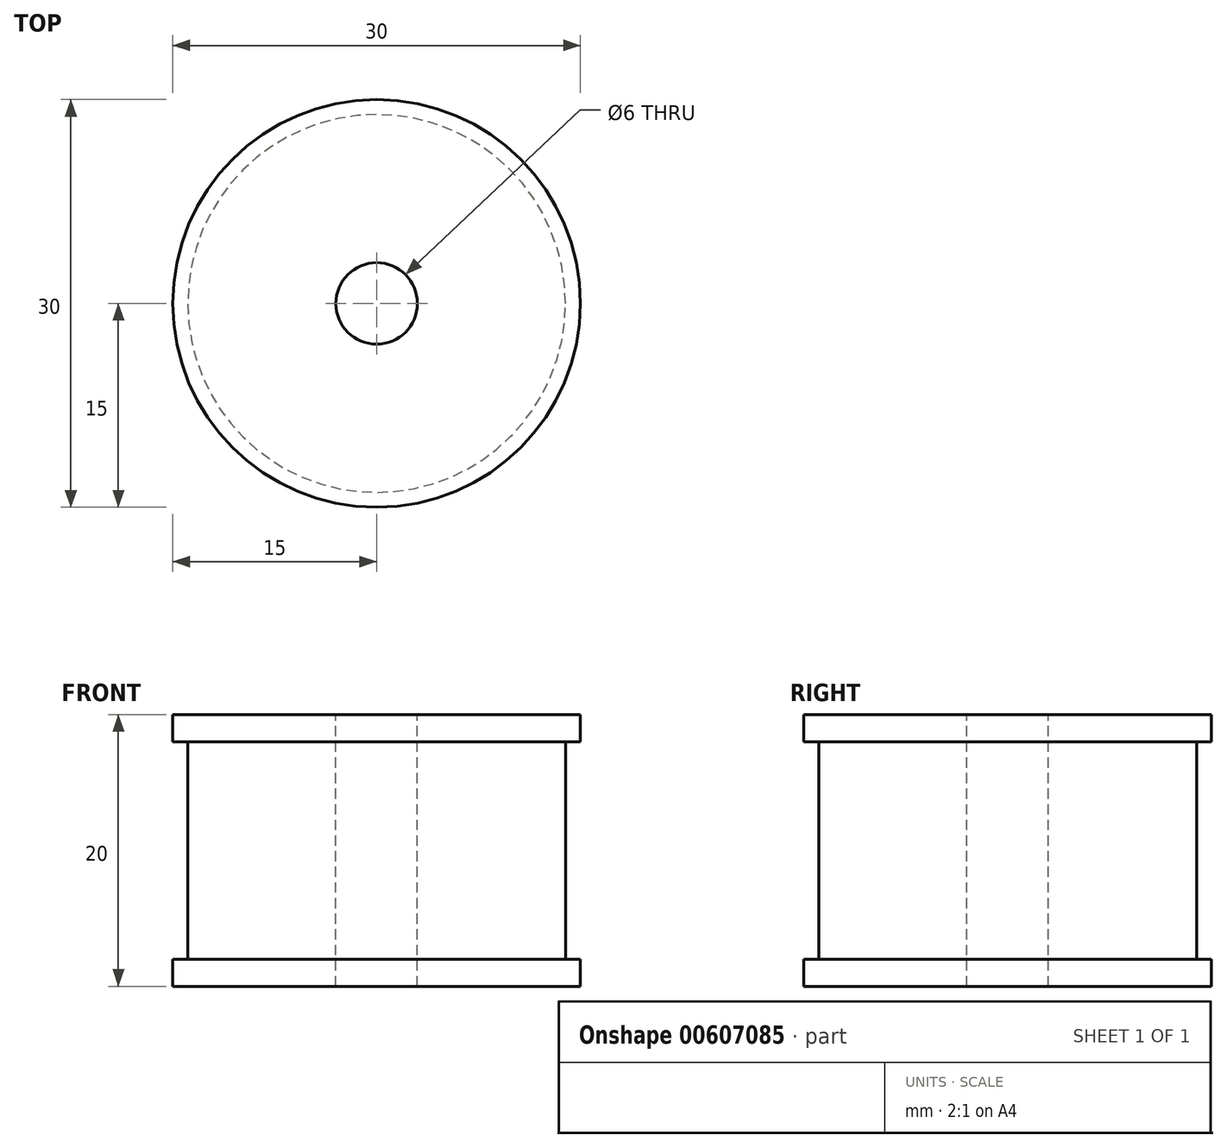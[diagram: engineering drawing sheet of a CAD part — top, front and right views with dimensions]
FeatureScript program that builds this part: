
annotation { "Feature Type Name" : "Feature", "Feature Type Description" : "" }
export const myFeature = defineFeature(function(context is Context, id is Id, definition is map)
    precondition{}
    {
        {
            var Q0;
            Q0=qCreatedBy(makeId("Top.planeOp"),FACE);
            var sketch = newSketch(context, id + "F0", { "sketchPlane" : qUnion([Q0]) });
            skCircle(sketch, "E0", {"center": v(0, 0) * mm, "radius": 13.9 * mm});
            skSolve(sketch);
        }
        {
            var Q0;
            Q0 = qSketchRegion(id + "F0", true);
            extrude(context, id + "F1", {"entities" : qUnion([Q0]), "depth" : 16 * mm, "offsetDistance" : 25 * mm});
        }
        {
            var Q0;
            Q0=makeQuery(id+"F1.opExtrude","CAP_FACE",FACE,{"disambiguationData":[OSD([sQuery(id+"F0.wireOp",EDGE,"E0")])],"isStart":false});
            var sketch = newSketch(context, id + "F2", { "sketchPlane" : qUnion([Q0]) });
            skCircle(sketch, "E1", {"center": v(0, 0) * mm, "radius": 15 * mm});
            skSolve(sketch);
        }
        {
            var Q0;
            Q0=makeQuery(id+"F2.imprint","IMPRINT",FACE,{"disambiguationData":[TD([[makeQuery(id+"F2.imprint","IMPRINT",EDGE,{"derivedFrom":makeQuery(id+"F1.opExtrude","CAP_EDGE",EDGE,{"disambiguationData":[OSD([sQuery(id+"F0.wireOp",EDGE,"E0")])],"isStart":false})}),1.0]])]});
            var Q1;
            Q1=makeQuery(id+"F2.imprint","IMPRINT",FACE,{"disambiguationData":[TD([[makeQuery(id+"F2.imprint","IMPRINT",EDGE,{"derivedFrom":sQuery(id+"F2.wireOp",EDGE,"E1")}),1.0]])]});
            extrude(context, id + "F3", {"entities" : qUnion([Q0, Q1]), "operationType" : NewBodyOperationType.ADD, "depth" : 2 * mm, "offsetDistance" : 25 * mm});
        }
        {
            var Q0;
            Q0=makeQuery(id+"F1.opExtrude","CAP_FACE",FACE,{"disambiguationData":[OSD([sQuery(id+"F0.wireOp",EDGE,"E0")])],"isStart":true});
            var sketch = newSketch(context, id + "F4", { "sketchPlane" : qUnion([Q0]) });
            skCircle(sketch, "E2", {"center": v(0, 0) * mm, "radius": 15 * mm});
            skSolve(sketch);
        }
        {
            var Q0;
            Q0 = qSketchRegion(id + "F4", true);
            extrude(context, id + "F5", {"entities" : qUnion([Q0]), "operationType" : NewBodyOperationType.ADD, "depth" : 2 * mm, "offsetDistance" : 25 * mm});
        }
        {
            var Q0;
            Q0=makeQuery(id+"F3.opExtrude","CAP_FACE",FACE,{"disambiguationData":[OSD([sQuery(id+"F2.wireOp",EDGE,"E1")])],"isStart":false});
            var sketch = newSketch(context, id + "F6", { "sketchPlane" : qUnion([Q0]) });
            skCircle(sketch, "E3", {"center": v(0, 0) * mm, "radius": 3 * mm});
            skSolve(sketch);
        }
        {
            var Q0;
            Q0 = qSketchRegion(id + "F6", true);
            extrude(context, id + "F7", {"entities" : qUnion([Q0]), "operationType" : NewBodyOperationType.REMOVE, "endBound" : BoundingType.THROUGH_ALL, "oppositeDirection" : true, "depth" : 25 * mm, "offsetDistance" : 25 * mm});
        }
    });
